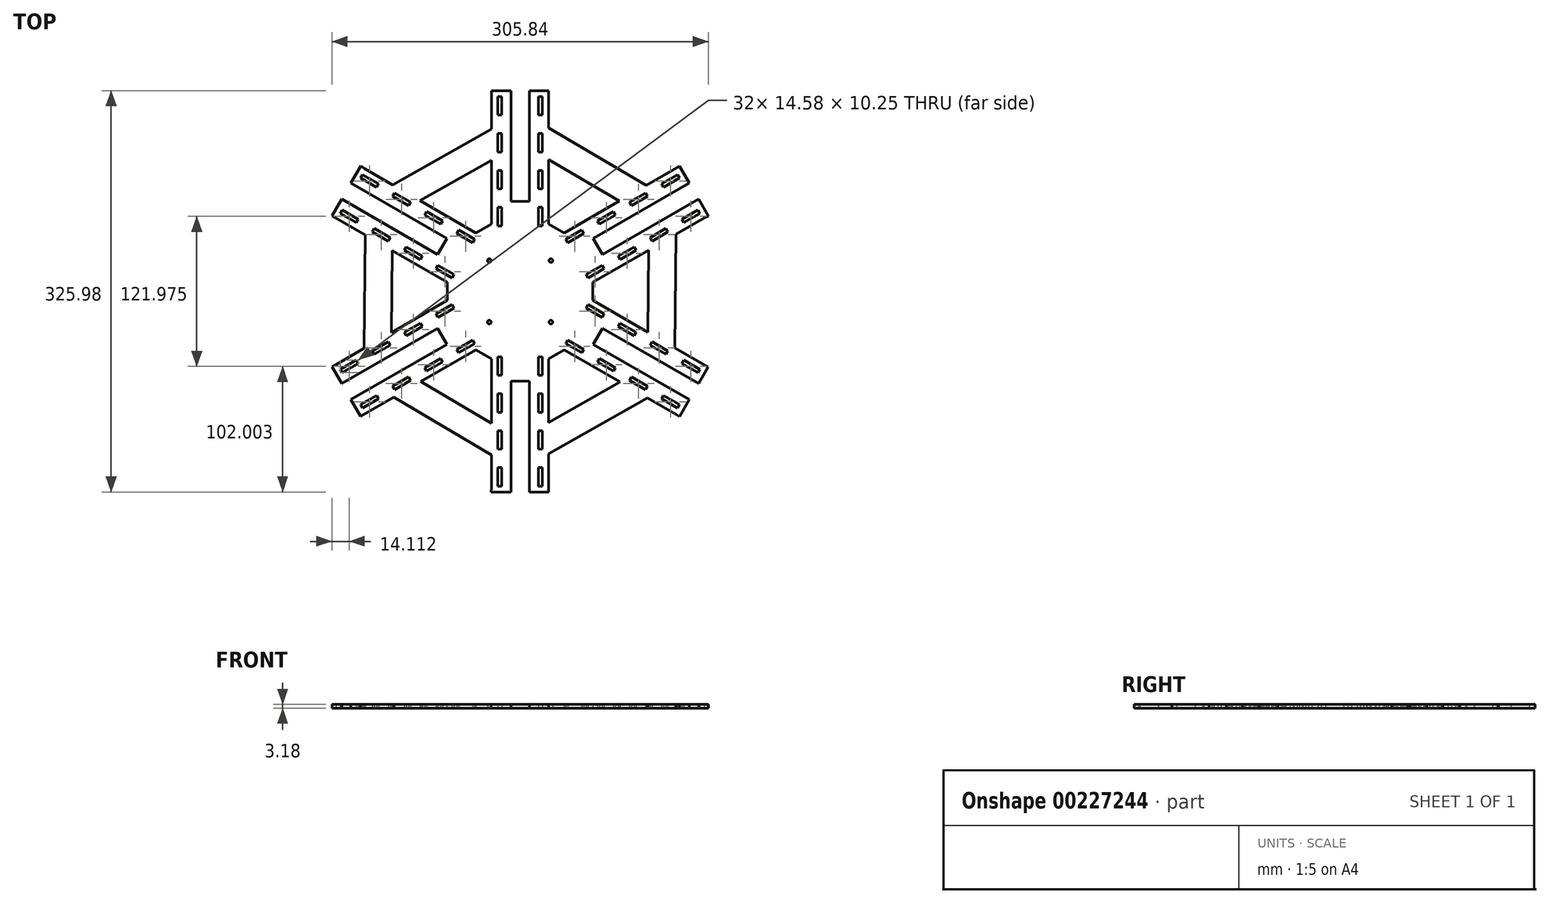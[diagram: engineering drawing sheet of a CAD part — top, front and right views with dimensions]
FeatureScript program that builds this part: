
annotation { "Feature Type Name" : "Feature", "Feature Type Description" : "" }
export const myFeature = defineFeature(function(context is Context, id is Id, definition is map)
    precondition{}
    {
        {
            var Q0;
            Q0=qCreatedBy(makeId("Top.planeOp"),FACE);
            var sketch = newSketch(context, id + "F0", { "sketchPlane" : qUnion([Q0])});
            skCircle(sketch, "E0.cCircle", {"center": v(0, 0) * mm, "radius": 173.2 * mm, "construction": true});
            skLineSegment(sketch, "E0.0", {"start": v(100, -173.2) * mm, "end": v(-100, -173.2) * mm});
            skLineSegment(sketch, "E0.1", {"start": v(-100, -173.2) * mm, "end": v(-200, 0) * mm});
            skLineSegment(sketch, "E0.2", {"start": v(-200, 0) * mm, "end": v(-100, 173.2) * mm});
            skLineSegment(sketch, "E0.3", {"start": v(-100, 173.2) * mm, "end": v(100, 173.2) * mm});
            skLineSegment(sketch, "E0.4", {"start": v(100, 173.2) * mm, "end": v(200, 0) * mm});
            skLineSegment(sketch, "E0.5", {"start": v(200, 0) * mm, "end": v(100, -173.2) * mm});
            skPoint(sketch, "E0.0.midPoint", {"position": v(0, -173.2) * mm});
            skLineSegment(sketch, "E1.bottom", {"start": v(-15, 143.2) * mm, "end": v(-18.18, 143.2) * mm});
            skLineSegment(sketch, "E1.top", {"start": v(-15, 158.2) * mm, "end": v(-18.18, 158.2) * mm});
            skLineSegment(sketch, "E1.left", {"start": v(-15, 143.2) * mm, "end": v(-15, 158.2) * mm});
            skLineSegment(sketch, "E1.right", {"start": v(-18.18, 143.2) * mm, "end": v(-18.18, 158.2) * mm});
            skPoint(sketch, "E1.middle", {"position": v(-16.59, 150.7) * mm});
            skPoint(sketch, "E2.0.1.0", {"position": v(-16.59, 120.7) * mm});
            skLineSegment(sketch, "E2.0.1.1", {"start": v(-18.18, 113.2) * mm, "end": v(-18.18, 128.2) * mm});
            skLineSegment(sketch, "E2.0.1.2", {"start": v(-15, 113.2) * mm, "end": v(-15, 128.2) * mm});
            skLineSegment(sketch, "E2.0.1.3", {"start": v(-15, 128.2) * mm, "end": v(-18.18, 128.2) * mm});
            skLineSegment(sketch, "E2.0.1.4", {"start": v(-15, 113.2) * mm, "end": v(-18.18, 113.2) * mm});
            skPoint(sketch, "E2.1.0.0", {"position": v(16.59, 150.7) * mm});
            skLineSegment(sketch, "E2.1.0.1", {"start": v(15, 143.2) * mm, "end": v(15, 158.2) * mm});
            skLineSegment(sketch, "E2.1.0.2", {"start": v(18.17, 143.2) * mm, "end": v(18.17, 158.2) * mm});
            skLineSegment(sketch, "E2.1.0.3", {"start": v(18.17, 158.2) * mm, "end": v(15, 158.2) * mm});
            skLineSegment(sketch, "E2.1.0.4", {"start": v(18.17, 143.2) * mm, "end": v(15, 143.2) * mm});
            skPoint(sketch, "E2.1.1.0", {"position": v(16.59, 120.7) * mm});
            skLineSegment(sketch, "E2.1.1.1", {"start": v(15, 113.2) * mm, "end": v(15, 128.2) * mm});
            skLineSegment(sketch, "E2.1.1.2", {"start": v(18.17, 113.2) * mm, "end": v(18.17, 128.2) * mm});
            skLineSegment(sketch, "E2.1.1.3", {"start": v(18.17, 128.2) * mm, "end": v(15, 128.2) * mm});
            skLineSegment(sketch, "E2.1.1.4", {"start": v(18.17, 113.2) * mm, "end": v(15, 113.2) * mm});
            skLineSegment(sketch, "E2.direction1", {"start": v(-18.18, 143.2) * mm, "end": v(15, 143.2) * mm, "construction": true});
            skLineSegment(sketch, "E2.direction2", {"start": v(-18.18, 143.2) * mm, "end": v(-18.18, 113.2) * mm, "construction": true});
            skLineSegment(sketch, "E3.1.0", {"start": v(-116.52, 84.6) * mm, "end": v(-129.5, 92.1) * mm});
            skLineSegment(sketch, "E3.1.1", {"start": v(-114.93, 87.34) * mm, "end": v(-127.92, 94.84) * mm});
            skPoint(sketch, "E3.1.2", {"position": v(-138.8, 60.99) * mm});
            skLineSegment(sketch, "E3.1.3", {"start": v(-133.1, 55.86) * mm, "end": v(-146.1, 63.36) * mm});
            skLineSegment(sketch, "E3.1.4", {"start": v(-131.52, 58.61) * mm, "end": v(-144.5, 66.11) * mm});
            skLineSegment(sketch, "E3.1.5", {"start": v(-107.13, 40.86) * mm, "end": v(-120.12, 48.36) * mm});
            skLineSegment(sketch, "E3.1.6", {"start": v(-133.1, 55.86) * mm, "end": v(-116.52, 84.6) * mm, "construction": true});
            skLineSegment(sketch, "E3.1.7", {"start": v(-105.54, 43.61) * mm, "end": v(-118.53, 51.11) * mm});
            skPoint(sketch, "E3.1.8", {"position": v(-122.22, 89.72) * mm});
            skLineSegment(sketch, "E3.1.9", {"start": v(-88.95, 72.34) * mm, "end": v(-101.94, 79.84) * mm});
            skLineSegment(sketch, "E3.1.10", {"start": v(-90.54, 69.6) * mm, "end": v(-103.53, 77.1) * mm});
            skLineSegment(sketch, "E3.1.11", {"start": v(-133.1, 55.86) * mm, "end": v(-107.13, 40.86) * mm, "construction": true});
            skPoint(sketch, "E3.1.12", {"position": v(-112.83, 45.99) * mm});
            skPoint(sketch, "E3.1.13", {"position": v(-96.24, 74.72) * mm});
            skLineSegment(sketch, "E3.1.14", {"start": v(-131.52, 58.61) * mm, "end": v(-133.1, 55.86) * mm});
            skLineSegment(sketch, "E3.1.15", {"start": v(-105.54, 43.61) * mm, "end": v(-107.13, 40.86) * mm});
            skLineSegment(sketch, "E3.1.16", {"start": v(-88.95, 72.34) * mm, "end": v(-90.54, 69.6) * mm});
            skLineSegment(sketch, "E3.1.17", {"start": v(-144.5, 66.11) * mm, "end": v(-146.1, 63.36) * mm});
            skLineSegment(sketch, "E3.1.18", {"start": v(-114.93, 87.34) * mm, "end": v(-116.52, 84.6) * mm});
            skLineSegment(sketch, "E3.1.19", {"start": v(-118.53, 51.11) * mm, "end": v(-120.12, 48.36) * mm});
            skLineSegment(sketch, "E3.1.20", {"start": v(-127.92, 94.84) * mm, "end": v(-129.5, 92.1) * mm});
            skLineSegment(sketch, "E3.1.21", {"start": v(-101.94, 79.84) * mm, "end": v(-103.53, 77.1) * mm});
            skLineSegment(sketch, "E3.2.0", {"start": v(-131.52, -58.61) * mm, "end": v(-144.5, -66.11) * mm});
            skLineSegment(sketch, "E3.2.1", {"start": v(-133.1, -55.86) * mm, "end": v(-146.1, -63.36) * mm});
            skPoint(sketch, "E3.2.2", {"position": v(-122.22, -89.72) * mm});
            skLineSegment(sketch, "E3.2.3", {"start": v(-114.93, -87.34) * mm, "end": v(-127.92, -94.84) * mm});
            skLineSegment(sketch, "E3.2.4", {"start": v(-116.52, -84.6) * mm, "end": v(-129.5, -92.1) * mm});
            skLineSegment(sketch, "E3.2.5", {"start": v(-88.95, -72.34) * mm, "end": v(-101.94, -79.84) * mm});
            skLineSegment(sketch, "E3.2.6", {"start": v(-114.93, -87.34) * mm, "end": v(-131.52, -58.61) * mm, "construction": true});
            skLineSegment(sketch, "E3.2.7", {"start": v(-90.54, -69.6) * mm, "end": v(-103.53, -77.1) * mm});
            skPoint(sketch, "E3.2.8", {"position": v(-138.8, -60.99) * mm});
            skLineSegment(sketch, "E3.2.9", {"start": v(-107.13, -40.86) * mm, "end": v(-120.12, -48.36) * mm});
            skLineSegment(sketch, "E3.2.10", {"start": v(-105.54, -43.61) * mm, "end": v(-118.53, -51.11) * mm});
            skLineSegment(sketch, "E3.2.11", {"start": v(-114.93, -87.34) * mm, "end": v(-88.95, -72.34) * mm, "construction": true});
            skPoint(sketch, "E3.2.12", {"position": v(-96.24, -74.72) * mm});
            skPoint(sketch, "E3.2.13", {"position": v(-112.83, -45.99) * mm});
            skLineSegment(sketch, "E3.2.14", {"start": v(-116.52, -84.6) * mm, "end": v(-114.93, -87.34) * mm});
            skLineSegment(sketch, "E3.2.15", {"start": v(-90.54, -69.6) * mm, "end": v(-88.95, -72.34) * mm});
            skLineSegment(sketch, "E3.2.16", {"start": v(-107.13, -40.86) * mm, "end": v(-105.54, -43.61) * mm});
            skLineSegment(sketch, "E3.2.17", {"start": v(-129.5, -92.1) * mm, "end": v(-127.92, -94.84) * mm});
            skLineSegment(sketch, "E3.2.18", {"start": v(-133.1, -55.86) * mm, "end": v(-131.52, -58.61) * mm});
            skLineSegment(sketch, "E3.2.19", {"start": v(-103.53, -77.1) * mm, "end": v(-101.94, -79.84) * mm});
            skLineSegment(sketch, "E3.2.20", {"start": v(-146.1, -63.36) * mm, "end": v(-144.5, -66.11) * mm});
            skLineSegment(sketch, "E3.2.21", {"start": v(-120.12, -48.36) * mm, "end": v(-118.53, -51.11) * mm});
            skLineSegment(sketch, "E3.3.0", {"start": v(-15, -143.2) * mm, "end": v(-15, -158.2) * mm});
            skLineSegment(sketch, "E3.3.1", {"start": v(-18.17, -143.2) * mm, "end": v(-18.17, -158.2) * mm});
            skPoint(sketch, "E3.3.2", {"position": v(16.59, -150.7) * mm});
            skLineSegment(sketch, "E3.3.3", {"start": v(18.18, -143.2) * mm, "end": v(18.18, -158.2) * mm});
            skLineSegment(sketch, "E3.3.4", {"start": v(15, -143.2) * mm, "end": v(15, -158.2) * mm});
            skLineSegment(sketch, "E3.3.5", {"start": v(18.18, -113.2) * mm, "end": v(18.18, -128.2) * mm});
            skLineSegment(sketch, "E3.3.6", {"start": v(18.17, -143.2) * mm, "end": v(-15, -143.2) * mm, "construction": true});
            skLineSegment(sketch, "E3.3.7", {"start": v(15, -113.2) * mm, "end": v(15, -128.2) * mm});
            skPoint(sketch, "E3.3.8", {"position": v(-16.59, -150.7) * mm});
            skLineSegment(sketch, "E3.3.9", {"start": v(-18.17, -113.2) * mm, "end": v(-18.17, -128.2) * mm});
            skLineSegment(sketch, "E3.3.10", {"start": v(-15, -113.2) * mm, "end": v(-15, -128.2) * mm});
            skLineSegment(sketch, "E3.3.11", {"start": v(18.18, -143.2) * mm, "end": v(18.18, -113.2) * mm, "construction": true});
            skPoint(sketch, "E3.3.12", {"position": v(16.59, -120.7) * mm});
            skPoint(sketch, "E3.3.13", {"position": v(-16.59, -120.7) * mm});
            skLineSegment(sketch, "E3.3.14", {"start": v(15, -143.2) * mm, "end": v(18.17, -143.2) * mm});
            skLineSegment(sketch, "E3.3.15", {"start": v(15, -113.2) * mm, "end": v(18.17, -113.2) * mm});
            skLineSegment(sketch, "E3.3.16", {"start": v(-18.18, -113.2) * mm, "end": v(-15, -113.2) * mm});
            skLineSegment(sketch, "E3.3.17", {"start": v(15, -158.2) * mm, "end": v(18.17, -158.2) * mm});
            skLineSegment(sketch, "E3.3.18", {"start": v(-18.18, -143.2) * mm, "end": v(-15, -143.2) * mm});
            skLineSegment(sketch, "E3.3.19", {"start": v(15, -128.2) * mm, "end": v(18.17, -128.2) * mm});
            skLineSegment(sketch, "E3.3.20", {"start": v(-18.18, -158.2) * mm, "end": v(-15, -158.2) * mm});
            skLineSegment(sketch, "E3.3.21", {"start": v(-18.18, -128.2) * mm, "end": v(-15, -128.2) * mm});
            skLineSegment(sketch, "E3.4.0", {"start": v(116.52, -84.6) * mm, "end": v(129.5, -92.1) * mm});
            skLineSegment(sketch, "E3.4.1", {"start": v(114.93, -87.34) * mm, "end": v(127.92, -94.84) * mm});
            skPoint(sketch, "E3.4.2", {"position": v(138.8, -60.99) * mm});
            skLineSegment(sketch, "E3.4.3", {"start": v(133.1, -55.86) * mm, "end": v(146.1, -63.36) * mm});
            skLineSegment(sketch, "E3.4.4", {"start": v(131.52, -58.61) * mm, "end": v(144.5, -66.11) * mm});
            skLineSegment(sketch, "E3.4.5", {"start": v(107.13, -40.86) * mm, "end": v(120.12, -48.36) * mm});
            skLineSegment(sketch, "E3.4.6", {"start": v(133.1, -55.86) * mm, "end": v(116.52, -84.6) * mm, "construction": true});
            skLineSegment(sketch, "E3.4.7", {"start": v(105.54, -43.61) * mm, "end": v(118.53, -51.11) * mm});
            skPoint(sketch, "E3.4.8", {"position": v(122.22, -89.72) * mm});
            skLineSegment(sketch, "E3.4.9", {"start": v(88.95, -72.34) * mm, "end": v(101.94, -79.84) * mm});
            skLineSegment(sketch, "E3.4.10", {"start": v(90.54, -69.6) * mm, "end": v(103.53, -77.1) * mm});
            skLineSegment(sketch, "E3.4.11", {"start": v(133.1, -55.86) * mm, "end": v(107.13, -40.86) * mm, "construction": true});
            skPoint(sketch, "E3.4.12", {"position": v(112.83, -45.99) * mm});
            skPoint(sketch, "E3.4.13", {"position": v(96.24, -74.72) * mm});
            skLineSegment(sketch, "E3.4.14", {"start": v(131.52, -58.61) * mm, "end": v(133.1, -55.86) * mm});
            skLineSegment(sketch, "E3.4.15", {"start": v(105.54, -43.61) * mm, "end": v(107.13, -40.86) * mm});
            skLineSegment(sketch, "E3.4.16", {"start": v(88.95, -72.34) * mm, "end": v(90.54, -69.6) * mm});
            skLineSegment(sketch, "E3.4.17", {"start": v(144.5, -66.11) * mm, "end": v(146.1, -63.36) * mm});
            skLineSegment(sketch, "E3.4.18", {"start": v(114.93, -87.34) * mm, "end": v(116.52, -84.6) * mm});
            skLineSegment(sketch, "E3.4.19", {"start": v(118.53, -51.11) * mm, "end": v(120.12, -48.36) * mm});
            skLineSegment(sketch, "E3.4.20", {"start": v(127.92, -94.84) * mm, "end": v(129.5, -92.1) * mm});
            skLineSegment(sketch, "E3.4.21", {"start": v(101.94, -79.84) * mm, "end": v(103.53, -77.1) * mm});
            skLineSegment(sketch, "E3.5.0", {"start": v(131.52, 58.61) * mm, "end": v(144.5, 66.11) * mm});
            skLineSegment(sketch, "E3.5.1", {"start": v(133.1, 55.86) * mm, "end": v(146.1, 63.36) * mm});
            skPoint(sketch, "E3.5.2", {"position": v(122.22, 89.72) * mm});
            skLineSegment(sketch, "E3.5.3", {"start": v(114.93, 87.34) * mm, "end": v(127.92, 94.84) * mm});
            skLineSegment(sketch, "E3.5.4", {"start": v(116.52, 84.6) * mm, "end": v(129.5, 92.1) * mm});
            skLineSegment(sketch, "E3.5.5", {"start": v(88.95, 72.34) * mm, "end": v(101.94, 79.84) * mm});
            skLineSegment(sketch, "E3.5.6", {"start": v(114.93, 87.34) * mm, "end": v(131.52, 58.61) * mm, "construction": true});
            skLineSegment(sketch, "E3.5.7", {"start": v(90.54, 69.6) * mm, "end": v(103.53, 77.1) * mm});
            skPoint(sketch, "E3.5.8", {"position": v(138.8, 60.99) * mm});
            skLineSegment(sketch, "E3.5.9", {"start": v(107.13, 40.86) * mm, "end": v(120.12, 48.36) * mm});
            skLineSegment(sketch, "E3.5.10", {"start": v(105.54, 43.61) * mm, "end": v(118.53, 51.11) * mm});
            skLineSegment(sketch, "E3.5.11", {"start": v(114.93, 87.34) * mm, "end": v(88.95, 72.34) * mm, "construction": true});
            skPoint(sketch, "E3.5.12", {"position": v(96.24, 74.72) * mm});
            skPoint(sketch, "E3.5.13", {"position": v(112.83, 45.99) * mm});
            skLineSegment(sketch, "E3.5.14", {"start": v(116.52, 84.6) * mm, "end": v(114.93, 87.34) * mm});
            skLineSegment(sketch, "E3.5.15", {"start": v(90.54, 69.6) * mm, "end": v(88.95, 72.34) * mm});
            skLineSegment(sketch, "E3.5.16", {"start": v(107.13, 40.86) * mm, "end": v(105.54, 43.61) * mm});
            skLineSegment(sketch, "E3.5.17", {"start": v(129.5, 92.1) * mm, "end": v(127.92, 94.84) * mm});
            skLineSegment(sketch, "E3.5.18", {"start": v(133.1, 55.86) * mm, "end": v(131.52, 58.61) * mm});
            skLineSegment(sketch, "E3.5.19", {"start": v(103.53, 77.1) * mm, "end": v(101.94, 79.84) * mm});
            skLineSegment(sketch, "E3.5.20", {"start": v(146.1, 63.36) * mm, "end": v(144.5, 66.11) * mm});
            skLineSegment(sketch, "E3.5.21", {"start": v(120.12, 48.36) * mm, "end": v(118.53, 51.11) * mm});
            skLineSegment(sketch, "E4.bottom", {"start": v(25, -25) * mm, "end": v(-25, -25) * mm, "construction": true});
            skLineSegment(sketch, "E4.top", {"start": v(25, 25) * mm, "end": v(-25, 25) * mm, "construction": true});
            skLineSegment(sketch, "E4.left", {"start": v(25, -25) * mm, "end": v(25, 25) * mm, "construction": true});
            skLineSegment(sketch, "E4.right", {"start": v(-25, -25) * mm, "end": v(-25, 25) * mm, "construction": true});
            skCircle(sketch, "E5", {"center": v(-25, 25) * mm, "radius": 1.5 * mm});
            skCircle(sketch, "E6.1.0", {"center": v(-25, -25) * mm, "radius": 1.5 * mm});
            skCircle(sketch, "E6.2.0", {"center": v(25, -25) * mm, "radius": 1.5 * mm});
            skCircle(sketch, "E6.3.0", {"center": v(25, 25) * mm, "radius": 1.5 * mm});
            skPoint(sketch, "E7.0.0.2", {"position": v(-16.59, 90.7) * mm});
            skLineSegment(sketch, "E7.1.0.2", {"start": v(-18.18, 83.2) * mm, "end": v(-18.18, 98.2) * mm});
            skLineSegment(sketch, "E7.4.0.2", {"start": v(-15, 83.2) * mm, "end": v(-15, 98.2) * mm});
            skLineSegment(sketch, "E7.7.0.2", {"start": v(-15, 98.2) * mm, "end": v(-18.18, 98.2) * mm});
            skLineSegment(sketch, "E7.10.0.2", {"start": v(-15, 83.2) * mm, "end": v(-18.18, 83.2) * mm});
            skPoint(sketch, "E7.0.1.2", {"position": v(16.59, 90.7) * mm});
            skLineSegment(sketch, "E7.1.1.2", {"start": v(15, 83.2) * mm, "end": v(15, 98.2) * mm});
            skLineSegment(sketch, "E7.4.1.2", {"start": v(18.17, 83.2) * mm, "end": v(18.17, 98.2) * mm});
            skLineSegment(sketch, "E7.7.1.2", {"start": v(18.17, 98.2) * mm, "end": v(15, 98.2) * mm});
            skLineSegment(sketch, "E7.10.1.2", {"start": v(18.17, 83.2) * mm, "end": v(15, 83.2) * mm});
            skPoint(sketch, "E8.0.0.3", {"position": v(-16.59, 60.7) * mm});
            skLineSegment(sketch, "E8.1.0.3", {"start": v(-18.18, 53.2) * mm, "end": v(-18.18, 68.2) * mm});
            skLineSegment(sketch, "E8.4.0.3", {"start": v(-15, 53.2) * mm, "end": v(-15, 68.2) * mm});
            skLineSegment(sketch, "E8.7.0.3", {"start": v(-15, 68.2) * mm, "end": v(-18.18, 68.2) * mm});
            skLineSegment(sketch, "E8.10.0.3", {"start": v(-15, 53.2) * mm, "end": v(-18.18, 53.2) * mm});
            skPoint(sketch, "E8.0.1.3", {"position": v(16.59, 60.7) * mm});
            skLineSegment(sketch, "E8.1.1.3", {"start": v(15, 53.2) * mm, "end": v(15, 68.2) * mm});
            skLineSegment(sketch, "E8.4.1.3", {"start": v(18.17, 53.2) * mm, "end": v(18.17, 68.2) * mm});
            skLineSegment(sketch, "E8.7.1.3", {"start": v(18.17, 68.2) * mm, "end": v(15, 68.2) * mm});
            skLineSegment(sketch, "E8.10.1.3", {"start": v(18.18, 53.2) * mm, "end": v(15, 53.2) * mm});
            skPoint(sketch, "E9.1.0", {"position": v(-60.87, 15.99) * mm});
            skPoint(sketch, "E9.1.1", {"position": v(-86.85, 30.99) * mm});
            skPoint(sketch, "E9.1.2", {"position": v(-44.28, 44.72) * mm});
            skPoint(sketch, "E9.1.3", {"position": v(-70.26, 59.72) * mm});
            skLineSegment(sketch, "E9.1.4", {"start": v(-55.16, 10.86) * mm, "end": v(-68.15, 18.36) * mm});
            skLineSegment(sketch, "E9.1.5", {"start": v(-36.99, 42.34) * mm, "end": v(-49.98, 49.84) * mm});
            skLineSegment(sketch, "E9.1.6", {"start": v(-79.56, 28.61) * mm, "end": v(-92.55, 36.11) * mm});
            skLineSegment(sketch, "E9.1.7", {"start": v(-64.56, 54.6) * mm, "end": v(-77.55, 62.1) * mm});
            skLineSegment(sketch, "E9.1.8", {"start": v(-62.97, 57.34) * mm, "end": v(-75.96, 64.84) * mm});
            skLineSegment(sketch, "E9.1.9", {"start": v(-53.58, 13.61) * mm, "end": v(-66.57, 21.11) * mm});
            skLineSegment(sketch, "E9.1.10", {"start": v(-38.58, 39.6) * mm, "end": v(-51.57, 47.1) * mm});
            skLineSegment(sketch, "E9.1.11", {"start": v(-81.15, 25.86) * mm, "end": v(-94.14, 33.36) * mm});
            skLineSegment(sketch, "E9.1.12", {"start": v(-79.56, 28.61) * mm, "end": v(-81.15, 25.86) * mm});
            skLineSegment(sketch, "E9.1.13", {"start": v(-62.97, 57.34) * mm, "end": v(-64.56, 54.6) * mm});
            skLineSegment(sketch, "E9.1.14", {"start": v(-49.98, 49.84) * mm, "end": v(-51.57, 47.1) * mm});
            skLineSegment(sketch, "E9.1.15", {"start": v(-36.99, 42.34) * mm, "end": v(-38.58, 39.6) * mm});
            skLineSegment(sketch, "E9.1.16", {"start": v(-75.96, 64.84) * mm, "end": v(-77.55, 62.1) * mm});
            skLineSegment(sketch, "E9.1.17", {"start": v(-92.55, 36.11) * mm, "end": v(-94.14, 33.36) * mm});
            skLineSegment(sketch, "E9.1.18", {"start": v(-53.58, 13.61) * mm, "end": v(-55.16, 10.86) * mm});
            skLineSegment(sketch, "E9.1.19", {"start": v(-66.57, 21.11) * mm, "end": v(-68.15, 18.36) * mm});
            skPoint(sketch, "E9.2.0", {"position": v(-44.28, -44.72) * mm});
            skPoint(sketch, "E9.2.1", {"position": v(-70.26, -59.72) * mm});
            skPoint(sketch, "E9.2.2", {"position": v(-60.87, -15.99) * mm});
            skPoint(sketch, "E9.2.3", {"position": v(-86.85, -30.99) * mm});
            skLineSegment(sketch, "E9.2.4", {"start": v(-36.99, -42.34) * mm, "end": v(-49.98, -49.84) * mm});
            skLineSegment(sketch, "E9.2.5", {"start": v(-55.16, -10.86) * mm, "end": v(-68.15, -18.36) * mm});
            skLineSegment(sketch, "E9.2.6", {"start": v(-64.56, -54.6) * mm, "end": v(-77.55, -62.1) * mm});
            skLineSegment(sketch, "E9.2.7", {"start": v(-79.56, -28.61) * mm, "end": v(-92.55, -36.11) * mm});
            skLineSegment(sketch, "E9.2.8", {"start": v(-81.15, -25.86) * mm, "end": v(-94.14, -33.36) * mm});
            skLineSegment(sketch, "E9.2.9", {"start": v(-38.58, -39.6) * mm, "end": v(-51.57, -47.1) * mm});
            skLineSegment(sketch, "E9.2.10", {"start": v(-53.58, -13.61) * mm, "end": v(-66.57, -21.11) * mm});
            skLineSegment(sketch, "E9.2.11", {"start": v(-62.97, -57.34) * mm, "end": v(-75.96, -64.84) * mm});
            skLineSegment(sketch, "E9.2.12", {"start": v(-64.56, -54.6) * mm, "end": v(-62.97, -57.34) * mm});
            skLineSegment(sketch, "E9.2.13", {"start": v(-81.15, -25.86) * mm, "end": v(-79.56, -28.61) * mm});
            skLineSegment(sketch, "E9.2.14", {"start": v(-68.15, -18.36) * mm, "end": v(-66.57, -21.11) * mm});
            skLineSegment(sketch, "E9.2.15", {"start": v(-55.16, -10.86) * mm, "end": v(-53.58, -13.61) * mm});
            skLineSegment(sketch, "E9.2.16", {"start": v(-94.14, -33.36) * mm, "end": v(-92.55, -36.11) * mm});
            skLineSegment(sketch, "E9.2.17", {"start": v(-77.55, -62.1) * mm, "end": v(-75.96, -64.84) * mm});
            skLineSegment(sketch, "E9.2.18", {"start": v(-38.58, -39.6) * mm, "end": v(-36.99, -42.34) * mm});
            skLineSegment(sketch, "E9.2.19", {"start": v(-51.57, -47.1) * mm, "end": v(-49.98, -49.84) * mm});
            skPoint(sketch, "E9.3.0", {"position": v(16.59, -60.7) * mm});
            skPoint(sketch, "E9.3.1", {"position": v(16.59, -90.7) * mm});
            skPoint(sketch, "E9.3.2", {"position": v(-16.59, -60.7) * mm});
            skPoint(sketch, "E9.3.3", {"position": v(-16.59, -90.7) * mm});
            skLineSegment(sketch, "E9.3.4", {"start": v(18.18, -53.2) * mm, "end": v(18.18, -68.2) * mm});
            skLineSegment(sketch, "E9.3.5", {"start": v(-18.17, -53.2) * mm, "end": v(-18.17, -68.2) * mm});
            skLineSegment(sketch, "E9.3.6", {"start": v(15, -83.2) * mm, "end": v(15, -98.2) * mm});
            skLineSegment(sketch, "E9.3.7", {"start": v(-15, -83.2) * mm, "end": v(-15, -98.2) * mm});
            skLineSegment(sketch, "E9.3.8", {"start": v(-18.17, -83.2) * mm, "end": v(-18.17, -98.2) * mm});
            skLineSegment(sketch, "E9.3.9", {"start": v(15, -53.2) * mm, "end": v(15, -68.2) * mm});
            skLineSegment(sketch, "E9.3.10", {"start": v(-15, -53.2) * mm, "end": v(-15, -68.2) * mm});
            skLineSegment(sketch, "E9.3.11", {"start": v(18.18, -83.2) * mm, "end": v(18.18, -98.2) * mm});
            skLineSegment(sketch, "E9.3.12", {"start": v(15, -83.2) * mm, "end": v(18.17, -83.2) * mm});
            skLineSegment(sketch, "E9.3.13", {"start": v(-18.18, -83.2) * mm, "end": v(-15, -83.2) * mm});
            skLineSegment(sketch, "E9.3.14", {"start": v(-18.18, -68.2) * mm, "end": v(-15, -68.2) * mm});
            skLineSegment(sketch, "E9.3.15", {"start": v(-18.18, -53.2) * mm, "end": v(-15, -53.2) * mm});
            skLineSegment(sketch, "E9.3.16", {"start": v(-18.18, -98.2) * mm, "end": v(-15, -98.2) * mm});
            skLineSegment(sketch, "E9.3.17", {"start": v(15, -98.2) * mm, "end": v(18.17, -98.2) * mm});
            skLineSegment(sketch, "E9.3.18", {"start": v(15, -53.2) * mm, "end": v(18.17, -53.2) * mm});
            skLineSegment(sketch, "E9.3.19", {"start": v(15, -68.2) * mm, "end": v(18.17, -68.2) * mm});
            skPoint(sketch, "E9.4.0", {"position": v(60.87, -15.99) * mm});
            skPoint(sketch, "E9.4.1", {"position": v(86.85, -30.99) * mm});
            skPoint(sketch, "E9.4.2", {"position": v(44.28, -44.72) * mm});
            skPoint(sketch, "E9.4.3", {"position": v(70.26, -59.72) * mm});
            skLineSegment(sketch, "E9.4.4", {"start": v(55.16, -10.86) * mm, "end": v(68.15, -18.36) * mm});
            skLineSegment(sketch, "E9.4.5", {"start": v(36.99, -42.34) * mm, "end": v(49.98, -49.84) * mm});
            skLineSegment(sketch, "E9.4.6", {"start": v(79.56, -28.61) * mm, "end": v(92.55, -36.11) * mm});
            skLineSegment(sketch, "E9.4.7", {"start": v(64.56, -54.6) * mm, "end": v(77.55, -62.1) * mm});
            skLineSegment(sketch, "E9.4.8", {"start": v(62.97, -57.34) * mm, "end": v(75.96, -64.84) * mm});
            skLineSegment(sketch, "E9.4.9", {"start": v(53.58, -13.61) * mm, "end": v(66.57, -21.11) * mm});
            skLineSegment(sketch, "E9.4.10", {"start": v(38.58, -39.6) * mm, "end": v(51.57, -47.1) * mm});
            skLineSegment(sketch, "E9.4.11", {"start": v(81.15, -25.86) * mm, "end": v(94.14, -33.36) * mm});
            skLineSegment(sketch, "E9.4.12", {"start": v(79.56, -28.61) * mm, "end": v(81.15, -25.86) * mm});
            skLineSegment(sketch, "E9.4.13", {"start": v(62.97, -57.34) * mm, "end": v(64.56, -54.6) * mm});
            skLineSegment(sketch, "E9.4.14", {"start": v(49.98, -49.84) * mm, "end": v(51.57, -47.1) * mm});
            skLineSegment(sketch, "E9.4.15", {"start": v(36.99, -42.34) * mm, "end": v(38.58, -39.6) * mm});
            skLineSegment(sketch, "E9.4.16", {"start": v(75.96, -64.84) * mm, "end": v(77.55, -62.1) * mm});
            skLineSegment(sketch, "E9.4.17", {"start": v(92.55, -36.11) * mm, "end": v(94.14, -33.36) * mm});
            skLineSegment(sketch, "E9.4.18", {"start": v(53.58, -13.61) * mm, "end": v(55.16, -10.86) * mm});
            skLineSegment(sketch, "E9.4.19", {"start": v(66.57, -21.11) * mm, "end": v(68.15, -18.36) * mm});
            skPoint(sketch, "E9.5.0", {"position": v(44.28, 44.72) * mm});
            skPoint(sketch, "E9.5.1", {"position": v(70.26, 59.72) * mm});
            skPoint(sketch, "E9.5.2", {"position": v(60.87, 15.99) * mm});
            skPoint(sketch, "E9.5.3", {"position": v(86.85, 30.99) * mm});
            skLineSegment(sketch, "E9.5.4", {"start": v(36.99, 42.34) * mm, "end": v(49.98, 49.84) * mm});
            skLineSegment(sketch, "E9.5.5", {"start": v(55.16, 10.86) * mm, "end": v(68.15, 18.36) * mm});
            skLineSegment(sketch, "E9.5.6", {"start": v(64.56, 54.6) * mm, "end": v(77.55, 62.1) * mm});
            skLineSegment(sketch, "E9.5.7", {"start": v(79.56, 28.61) * mm, "end": v(92.55, 36.11) * mm});
            skLineSegment(sketch, "E9.5.8", {"start": v(81.15, 25.86) * mm, "end": v(94.14, 33.36) * mm});
            skLineSegment(sketch, "E9.5.9", {"start": v(38.58, 39.6) * mm, "end": v(51.57, 47.1) * mm});
            skLineSegment(sketch, "E9.5.10", {"start": v(53.58, 13.61) * mm, "end": v(66.57, 21.11) * mm});
            skLineSegment(sketch, "E9.5.11", {"start": v(62.97, 57.34) * mm, "end": v(75.96, 64.84) * mm});
            skLineSegment(sketch, "E9.5.12", {"start": v(64.56, 54.6) * mm, "end": v(62.97, 57.34) * mm});
            skLineSegment(sketch, "E9.5.13", {"start": v(81.15, 25.86) * mm, "end": v(79.56, 28.61) * mm});
            skLineSegment(sketch, "E9.5.14", {"start": v(68.15, 18.36) * mm, "end": v(66.57, 21.11) * mm});
            skLineSegment(sketch, "E9.5.15", {"start": v(55.16, 10.86) * mm, "end": v(53.58, 13.61) * mm});
            skLineSegment(sketch, "E9.5.16", {"start": v(94.14, 33.36) * mm, "end": v(92.55, 36.11) * mm});
            skLineSegment(sketch, "E9.5.17", {"start": v(77.55, 62.1) * mm, "end": v(75.96, 64.84) * mm});
            skLineSegment(sketch, "E9.5.18", {"start": v(38.58, 39.6) * mm, "end": v(36.99, 42.34) * mm});
            skLineSegment(sketch, "E9.5.19", {"start": v(51.57, 47.1) * mm, "end": v(49.98, 49.84) * mm});
            skLineSegment(sketch, "E10", {"start": v(-126.5, 99.8) * mm, "end": v(-35.78, 47.42) * mm});
            skLineSegment(sketch, "E11", {"start": v(-35.78, 47.42) * mm, "end": v(-23.17, 54.7) * mm});
            skLineSegment(sketch, "E12", {"start": v(-23.18, 54.7) * mm, "end": v(-23.18, 158.2) * mm});
            skLineSegment(sketch, "E13", {"start": v(-23.17, 158.2) * mm, "end": v(-126.5, 99.8) * mm});
            skLineSegment(sketch, "E14.1.0", {"start": v(-148.6, 59.03) * mm, "end": v(-149.68, -59.66) * mm});
            skLineSegment(sketch, "E14.1.1", {"start": v(-58.95, 7.28) * mm, "end": v(-148.6, 59.03) * mm});
            skLineSegment(sketch, "E14.1.2", {"start": v(-149.68, -59.66) * mm, "end": v(-58.95, -7.28) * mm});
            skLineSegment(sketch, "E14.1.3", {"start": v(-58.95, -7.28) * mm, "end": v(-58.95, 7.28) * mm});
            skLineSegment(sketch, "E14.2.0", {"start": v(-125.42, -99.17) * mm, "end": v(-23.18, -159.46) * mm});
            skLineSegment(sketch, "E14.2.1", {"start": v(-35.78, -47.42) * mm, "end": v(-125.42, -99.17) * mm});
            skLineSegment(sketch, "E14.2.2", {"start": v(-23.18, -159.46) * mm, "end": v(-23.18, -54.7) * mm});
            skLineSegment(sketch, "E14.2.3", {"start": v(-23.18, -54.7) * mm, "end": v(-35.78, -47.42) * mm});
            skLineSegment(sketch, "E14.3.0", {"start": v(23.17, -158.2) * mm, "end": v(126.5, -99.8) * mm});
            skLineSegment(sketch, "E14.3.1", {"start": v(23.17, -54.7) * mm, "end": v(23.17, -158.2) * mm});
            skLineSegment(sketch, "E14.3.2", {"start": v(126.5, -99.8) * mm, "end": v(35.78, -47.42) * mm});
            skLineSegment(sketch, "E14.3.3", {"start": v(35.78, -47.42) * mm, "end": v(23.17, -54.7) * mm});
            skLineSegment(sketch, "E14.4.0", {"start": v(148.6, -59.03) * mm, "end": v(149.68, 59.66) * mm});
            skLineSegment(sketch, "E14.4.1", {"start": v(58.95, -7.28) * mm, "end": v(148.6, -59.03) * mm});
            skLineSegment(sketch, "E14.4.2", {"start": v(149.68, 59.66) * mm, "end": v(58.95, 7.28) * mm});
            skLineSegment(sketch, "E14.4.3", {"start": v(58.95, 7.28) * mm, "end": v(58.95, -7.28) * mm});
            skLineSegment(sketch, "E14.5.0", {"start": v(125.42, 99.17) * mm, "end": v(23.17, 159.46) * mm});
            skLineSegment(sketch, "E14.5.1", {"start": v(35.78, 47.42) * mm, "end": v(125.42, 99.17) * mm});
            skLineSegment(sketch, "E14.5.2", {"start": v(23.17, 159.46) * mm, "end": v(23.18, 54.7) * mm});
            skLineSegment(sketch, "E14.5.3", {"start": v(23.18, 54.7) * mm, "end": v(35.78, 47.42) * mm});
            skLineSegment(sketch, "E15", {"start": v(-103.5, 86.51) * mm, "end": v(-23.18, 131.91) * mm});
            skLineSegment(sketch, "E16", {"start": v(-23.18, 131.91) * mm, "end": v(-23.18, 106.45) * mm});
            skLineSegment(sketch, "E17", {"start": v(-23.18, 106.45) * mm, "end": v(-81.21, 73.65) * mm});
            skLineSegment(sketch, "E18.1.0", {"start": v(-126.67, -46.37) * mm, "end": v(-125.83, 45.89) * mm});
            skLineSegment(sketch, "E18.1.1", {"start": v(-103.77, 33.15) * mm, "end": v(-104.39, -33.5) * mm});
            skLineSegment(sketch, "E18.2.0", {"start": v(-23.18, -132.89) * mm, "end": v(-102.65, -86.03) * mm});
            skLineSegment(sketch, "E18.2.1", {"start": v(-80.6, -73.3) * mm, "end": v(-23.17, -107.15) * mm});
            skLineSegment(sketch, "E19.1.3.0", {"start": v(103.5, -86.51) * mm, "end": v(23.17, -131.91) * mm});
            skLineSegment(sketch, "E19.3.3.0", {"start": v(23.17, -106.45) * mm, "end": v(81.21, -73.65) * mm});
            skLineSegment(sketch, "E19.1.4.0", {"start": v(126.67, 46.37) * mm, "end": v(125.83, -45.89) * mm});
            skLineSegment(sketch, "E19.3.4.0", {"start": v(103.77, -33.15) * mm, "end": v(104.39, 33.5) * mm});
            skLineSegment(sketch, "E19.1.5.0", {"start": v(23.17, 132.89) * mm, "end": v(102.65, 86.03) * mm});
            skLineSegment(sketch, "E19.3.5.0", {"start": v(80.6, 73.3) * mm, "end": v(23.17, 107.15) * mm});
            skLineSegment(sketch, "E20", {"start": v(-148.6, 59.03) * mm, "end": v(-152.74, 61.42) * mm});
            skLineSegment(sketch, "E21", {"start": v(-152.74, 61.42) * mm, "end": v(-129.39, 101.87) * mm});
            skLineSegment(sketch, "E22", {"start": v(-129.39, 101.87) * mm, "end": v(-126.5, 99.8) * mm});
            skLineSegment(sketch, "E23.1.0", {"start": v(-129.57, -101.56) * mm, "end": v(-152.92, -61.12) * mm});
            skLineSegment(sketch, "E23.1.1", {"start": v(-152.92, -61.12) * mm, "end": v(-149.68, -59.66) * mm});
            skLineSegment(sketch, "E23.1.2", {"start": v(-125.42, -99.17) * mm, "end": v(-129.57, -101.56) * mm});
            skLineSegment(sketch, "E23.2.0", {"start": v(23.17, -162.99) * mm, "end": v(-23.53, -162.99) * mm});
            skLineSegment(sketch, "E23.2.1", {"start": v(-23.53, -162.99) * mm, "end": v(-23.18, -159.46) * mm});
            skLineSegment(sketch, "E23.2.2", {"start": v(23.17, -158.2) * mm, "end": v(23.17, -162.99) * mm});
            skLineSegment(sketch, "E23.3.0", {"start": v(152.74, -61.42) * mm, "end": v(129.39, -101.87) * mm});
            skLineSegment(sketch, "E23.3.1", {"start": v(129.39, -101.87) * mm, "end": v(126.5, -99.8) * mm});
            skLineSegment(sketch, "E23.3.2", {"start": v(148.6, -59.03) * mm, "end": v(152.74, -61.42) * mm});
            skLineSegment(sketch, "E23.4.0", {"start": v(129.57, 101.56) * mm, "end": v(152.92, 61.12) * mm});
            skLineSegment(sketch, "E23.4.1", {"start": v(152.92, 61.12) * mm, "end": v(149.68, 59.66) * mm});
            skLineSegment(sketch, "E23.4.2", {"start": v(125.42, 99.17) * mm, "end": v(129.57, 101.56) * mm});
            skLineSegment(sketch, "E23.5.2", {"start": v(-23.18, 158.2) * mm, "end": v(-23.18, 162.99) * mm});
            skLineSegment(sketch, "E24", {"start": v(23.17, 159.46) * mm, "end": v(23.17, 162.99) * mm});
            skLineSegment(sketch, "E25", {"start": v(23.17, 162.99) * mm, "end": v(-23.18, 162.99) * mm});
            skSolve(sketch);
        }
        {
            var Q0;
            {var subQ0=sQuery(id+"F0.wireOp",EDGE,"E15");Q0=makeQuery(id+"F0.imprint","IMPRINT",FACE,{"disambiguationData":[TD([[makeQuery(id+"F0.imprint","IMPRINT",EDGE,{"derivedFrom":subQ0}),-1.0]])]});}
            var Q1;
            {var subQ0=sQuery(id+"F0.wireOp",EDGE,"E18.1.0");Q1=makeQuery(id+"F0.imprint","IMPRINT",FACE,{"disambiguationData":[TD([[makeQuery(id+"F0.imprint","IMPRINT",EDGE,{"derivedFrom":subQ0}),-1.0]])]});}
            var Q2;
            {var subQ0=sQuery(id+"F0.wireOp",EDGE,"E18.2.0");Q2=makeQuery(id+"F0.imprint","IMPRINT",FACE,{"disambiguationData":[TD([[makeQuery(id+"F0.imprint","IMPRINT",EDGE,{"derivedFrom":subQ0}),-1.0]])]});}
            var Q3;
            {var subQ0=sQuery(id+"F0.wireOp",EDGE,"E19.1.3.0");Q3=makeQuery(id+"F0.imprint","IMPRINT",FACE,{"disambiguationData":[TD([[makeQuery(id+"F0.imprint","IMPRINT",EDGE,{"derivedFrom":subQ0}),-1.0]])]});}
            var Q4;
            {var subQ0=sQuery(id+"F0.wireOp",EDGE,"E19.1.4.0");Q4=makeQuery(id+"F0.imprint","IMPRINT",FACE,{"disambiguationData":[TD([[makeQuery(id+"F0.imprint","IMPRINT",EDGE,{"derivedFrom":subQ0}),-1.0]])]});}
            var Q5;
            {var subQ0=sQuery(id+"F0.wireOp",EDGE,"E19.1.5.0");Q5=makeQuery(id+"F0.imprint","IMPRINT",FACE,{"disambiguationData":[TD([[makeQuery(id+"F0.imprint","IMPRINT",EDGE,{"derivedFrom":subQ0}),-1.0]])]});}
            var Q6;
            Q6=makeQuery(id+"F0.imprint","IMPRINT",FACE,{"disambiguationData":[TD([[makeQuery(id+"F0.imprint","IMPRINT",EDGE,{"derivedFrom":sQuery(id+"F0.wireOp",EDGE,"E1.bottom")}),1.0]])]});
            extrude(context, id + "F1", {"entities" : qUnion([Q0, Q1, Q2, Q3, Q4, Q5, Q6]), "depth" : 3.17 * mm});
        }
        {
            var Q0;
            Q0=makeQuery(id+"F1.opExtrude","CAP_FACE",FACE,{"disambiguationData":[OSD([sQuery(id+"F0.wireOp",EDGE,"E1.bottom"),sQuery(id+"F0.wireOp",EDGE,"E1.top"),sQuery(id+"F0.wireOp",EDGE,"E1.left"),sQuery(id+"F0.wireOp",EDGE,"E1.right"),sQuery(id+"F0.wireOp",EDGE,"E2.0.1.1"),sQuery(id+"F0.wireOp",EDGE,"E2.0.1.2"),sQuery(id+"F0.wireOp",EDGE,"E2.0.1.3"),sQuery(id+"F0.wireOp",EDGE,"E2.0.1.4"),sQuery(id+"F0.wireOp",EDGE,"E2.1.0.1"),sQuery(id+"F0.wireOp",EDGE,"E2.1.0.2"),sQuery(id+"F0.wireOp",EDGE,"E2.1.0.3"),sQuery(id+"F0.wireOp",EDGE,"E2.1.0.4"),sQuery(id+"F0.wireOp",EDGE,"E2.1.1.1"),sQuery(id+"F0.wireOp",EDGE,"E2.1.1.2"),sQuery(id+"F0.wireOp",EDGE,"E2.1.1.3"),sQuery(id+"F0.wireOp",EDGE,"E2.1.1.4"),sQuery(id+"F0.wireOp",EDGE,"E3.1.0"),sQuery(id+"F0.wireOp",EDGE,"E3.1.1"),sQuery(id+"F0.wireOp",EDGE,"E3.1.3"),sQuery(id+"F0.wireOp",EDGE,"E3.1.4"),sQuery(id+"F0.wireOp",EDGE,"E3.1.5"),sQuery(id+"F0.wireOp",EDGE,"E3.1.7"),sQuery(id+"F0.wireOp",EDGE,"E3.1.9"),sQuery(id+"F0.wireOp",EDGE,"E3.1.10"),sQuery(id+"F0.wireOp",EDGE,"E3.1.14"),sQuery(id+"F0.wireOp",EDGE,"E3.1.15"),sQuery(id+"F0.wireOp",EDGE,"E3.1.16"),sQuery(id+"F0.wireOp",EDGE,"E3.1.17"),sQuery(id+"F0.wireOp",EDGE,"E3.1.18"),sQuery(id+"F0.wireOp",EDGE,"E3.1.19"),sQuery(id+"F0.wireOp",EDGE,"E3.1.20"),sQuery(id+"F0.wireOp",EDGE,"E3.1.21"),sQuery(id+"F0.wireOp",EDGE,"E3.2.0"),sQuery(id+"F0.wireOp",EDGE,"E3.2.1"),sQuery(id+"F0.wireOp",EDGE,"E3.2.3"),sQuery(id+"F0.wireOp",EDGE,"E3.2.4"),sQuery(id+"F0.wireOp",EDGE,"E3.2.5"),sQuery(id+"F0.wireOp",EDGE,"E3.2.7"),sQuery(id+"F0.wireOp",EDGE,"E3.2.9"),sQuery(id+"F0.wireOp",EDGE,"E3.2.10"),sQuery(id+"F0.wireOp",EDGE,"E3.2.14"),sQuery(id+"F0.wireOp",EDGE,"E3.2.15"),sQuery(id+"F0.wireOp",EDGE,"E3.2.16"),sQuery(id+"F0.wireOp",EDGE,"E3.2.17"),sQuery(id+"F0.wireOp",EDGE,"E3.2.18"),sQuery(id+"F0.wireOp",EDGE,"E3.2.19"),sQuery(id+"F0.wireOp",EDGE,"E3.2.20"),sQuery(id+"F0.wireOp",EDGE,"E3.2.21"),sQuery(id+"F0.wireOp",EDGE,"E3.3.0"),sQuery(id+"F0.wireOp",EDGE,"E3.3.1"),sQuery(id+"F0.wireOp",EDGE,"E3.3.3"),sQuery(id+"F0.wireOp",EDGE,"E3.3.4"),sQuery(id+"F0.wireOp",EDGE,"E3.3.5"),sQuery(id+"F0.wireOp",EDGE,"E3.3.7"),sQuery(id+"F0.wireOp",EDGE,"E3.3.9"),sQuery(id+"F0.wireOp",EDGE,"E3.3.10"),sQuery(id+"F0.wireOp",EDGE,"E3.3.14"),sQuery(id+"F0.wireOp",EDGE,"E3.3.15"),sQuery(id+"F0.wireOp",EDGE,"E3.3.16"),sQuery(id+"F0.wireOp",EDGE,"E3.3.17"),sQuery(id+"F0.wireOp",EDGE,"E3.3.18"),sQuery(id+"F0.wireOp",EDGE,"E3.3.19"),sQuery(id+"F0.wireOp",EDGE,"E3.3.20"),sQuery(id+"F0.wireOp",EDGE,"E3.3.21"),sQuery(id+"F0.wireOp",EDGE,"E3.4.0"),sQuery(id+"F0.wireOp",EDGE,"E3.4.1"),sQuery(id+"F0.wireOp",EDGE,"E3.4.3"),sQuery(id+"F0.wireOp",EDGE,"E3.4.4"),sQuery(id+"F0.wireOp",EDGE,"E3.4.5"),sQuery(id+"F0.wireOp",EDGE,"E3.4.7"),sQuery(id+"F0.wireOp",EDGE,"E3.4.9"),sQuery(id+"F0.wireOp",EDGE,"E3.4.10"),sQuery(id+"F0.wireOp",EDGE,"E3.4.14"),sQuery(id+"F0.wireOp",EDGE,"E3.4.15"),sQuery(id+"F0.wireOp",EDGE,"E3.4.16"),sQuery(id+"F0.wireOp",EDGE,"E3.4.17"),sQuery(id+"F0.wireOp",EDGE,"E3.4.18"),sQuery(id+"F0.wireOp",EDGE,"E3.4.19"),sQuery(id+"F0.wireOp",EDGE,"E3.4.20"),sQuery(id+"F0.wireOp",EDGE,"E3.4.21"),sQuery(id+"F0.wireOp",EDGE,"E3.5.0"),sQuery(id+"F0.wireOp",EDGE,"E3.5.1"),sQuery(id+"F0.wireOp",EDGE,"E3.5.3"),sQuery(id+"F0.wireOp",EDGE,"E3.5.4"),sQuery(id+"F0.wireOp",EDGE,"E3.5.5"),sQuery(id+"F0.wireOp",EDGE,"E3.5.7"),sQuery(id+"F0.wireOp",EDGE,"E3.5.9"),sQuery(id+"F0.wireOp",EDGE,"E3.5.10"),sQuery(id+"F0.wireOp",EDGE,"E3.5.14"),sQuery(id+"F0.wireOp",EDGE,"E3.5.15"),sQuery(id+"F0.wireOp",EDGE,"E3.5.16"),sQuery(id+"F0.wireOp",EDGE,"E3.5.17"),sQuery(id+"F0.wireOp",EDGE,"E3.5.18"),sQuery(id+"F0.wireOp",EDGE,"E3.5.19"),sQuery(id+"F0.wireOp",EDGE,"E3.5.20"),sQuery(id+"F0.wireOp",EDGE,"E3.5.21"),sQuery(id+"F0.wireOp",EDGE,"E5"),sQuery(id+"F0.wireOp",EDGE,"E6.1.0"),sQuery(id+"F0.wireOp",EDGE,"E6.2.0"),sQuery(id+"F0.wireOp",EDGE,"E6.3.0"),sQuery(id+"F0.wireOp",EDGE,"E7.1.0.2"),sQuery(id+"F0.wireOp",EDGE,"E7.4.0.2"),sQuery(id+"F0.wireOp",EDGE,"E7.7.0.2"),sQuery(id+"F0.wireOp",EDGE,"E7.10.0.2"),sQuery(id+"F0.wireOp",EDGE,"E7.1.1.2"),sQuery(id+"F0.wireOp",EDGE,"E7.4.1.2"),sQuery(id+"F0.wireOp",EDGE,"E7.7.1.2"),sQuery(id+"F0.wireOp",EDGE,"E7.10.1.2"),sQuery(id+"F0.wireOp",EDGE,"E8.1.0.3"),sQuery(id+"F0.wireOp",EDGE,"E8.4.0.3"),sQuery(id+"F0.wireOp",EDGE,"E8.7.0.3"),sQuery(id+"F0.wireOp",EDGE,"E8.10.0.3"),sQuery(id+"F0.wireOp",EDGE,"E8.1.1.3"),sQuery(id+"F0.wireOp",EDGE,"E8.4.1.3"),sQuery(id+"F0.wireOp",EDGE,"E8.7.1.3"),sQuery(id+"F0.wireOp",EDGE,"E8.10.1.3"),sQuery(id+"F0.wireOp",EDGE,"E9.1.4"),sQuery(id+"F0.wireOp",EDGE,"E9.1.5"),sQuery(id+"F0.wireOp",EDGE,"E9.1.6"),sQuery(id+"F0.wireOp",EDGE,"E9.1.7"),sQuery(id+"F0.wireOp",EDGE,"E9.1.8"),sQuery(id+"F0.wireOp",EDGE,"E9.1.9"),sQuery(id+"F0.wireOp",EDGE,"E9.1.10"),sQuery(id+"F0.wireOp",EDGE,"E9.1.11"),sQuery(id+"F0.wireOp",EDGE,"E9.1.12"),sQuery(id+"F0.wireOp",EDGE,"E9.1.13"),sQuery(id+"F0.wireOp",EDGE,"E9.1.14"),sQuery(id+"F0.wireOp",EDGE,"E9.1.15"),sQuery(id+"F0.wireOp",EDGE,"E9.1.16"),sQuery(id+"F0.wireOp",EDGE,"E9.1.17"),sQuery(id+"F0.wireOp",EDGE,"E9.1.18"),sQuery(id+"F0.wireOp",EDGE,"E9.1.19"),sQuery(id+"F0.wireOp",EDGE,"E9.2.4"),sQuery(id+"F0.wireOp",EDGE,"E9.2.5"),sQuery(id+"F0.wireOp",EDGE,"E9.2.6"),sQuery(id+"F0.wireOp",EDGE,"E9.2.7"),sQuery(id+"F0.wireOp",EDGE,"E9.2.8"),sQuery(id+"F0.wireOp",EDGE,"E9.2.9"),sQuery(id+"F0.wireOp",EDGE,"E9.2.10"),sQuery(id+"F0.wireOp",EDGE,"E9.2.11"),sQuery(id+"F0.wireOp",EDGE,"E9.2.12"),sQuery(id+"F0.wireOp",EDGE,"E9.2.13"),sQuery(id+"F0.wireOp",EDGE,"E9.2.14"),sQuery(id+"F0.wireOp",EDGE,"E9.2.15"),sQuery(id+"F0.wireOp",EDGE,"E9.2.16"),sQuery(id+"F0.wireOp",EDGE,"E9.2.17"),sQuery(id+"F0.wireOp",EDGE,"E9.2.18"),sQuery(id+"F0.wireOp",EDGE,"E9.2.19"),sQuery(id+"F0.wireOp",EDGE,"E9.3.4"),sQuery(id+"F0.wireOp",EDGE,"E9.3.5"),sQuery(id+"F0.wireOp",EDGE,"E9.3.6"),sQuery(id+"F0.wireOp",EDGE,"E9.3.7"),sQuery(id+"F0.wireOp",EDGE,"E9.3.8"),sQuery(id+"F0.wireOp",EDGE,"E9.3.9"),sQuery(id+"F0.wireOp",EDGE,"E9.3.10"),sQuery(id+"F0.wireOp",EDGE,"E9.3.11"),sQuery(id+"F0.wireOp",EDGE,"E9.3.12"),sQuery(id+"F0.wireOp",EDGE,"E9.3.13"),sQuery(id+"F0.wireOp",EDGE,"E9.3.14"),sQuery(id+"F0.wireOp",EDGE,"E9.3.15"),sQuery(id+"F0.wireOp",EDGE,"E9.3.16"),sQuery(id+"F0.wireOp",EDGE,"E9.3.17"),sQuery(id+"F0.wireOp",EDGE,"E9.3.18"),sQuery(id+"F0.wireOp",EDGE,"E9.3.19"),sQuery(id+"F0.wireOp",EDGE,"E9.4.4"),sQuery(id+"F0.wireOp",EDGE,"E9.4.5"),sQuery(id+"F0.wireOp",EDGE,"E9.4.6"),sQuery(id+"F0.wireOp",EDGE,"E9.4.7"),sQuery(id+"F0.wireOp",EDGE,"E9.4.8"),sQuery(id+"F0.wireOp",EDGE,"E9.4.9"),sQuery(id+"F0.wireOp",EDGE,"E9.4.10"),sQuery(id+"F0.wireOp",EDGE,"E9.4.11"),sQuery(id+"F0.wireOp",EDGE,"E9.4.12"),sQuery(id+"F0.wireOp",EDGE,"E9.4.13"),sQuery(id+"F0.wireOp",EDGE,"E9.4.14"),sQuery(id+"F0.wireOp",EDGE,"E9.4.15"),sQuery(id+"F0.wireOp",EDGE,"E9.4.16"),sQuery(id+"F0.wireOp",EDGE,"E9.4.17"),sQuery(id+"F0.wireOp",EDGE,"E9.4.18"),sQuery(id+"F0.wireOp",EDGE,"E9.4.19"),sQuery(id+"F0.wireOp",EDGE,"E9.5.4"),sQuery(id+"F0.wireOp",EDGE,"E9.5.5"),sQuery(id+"F0.wireOp",EDGE,"E9.5.6"),sQuery(id+"F0.wireOp",EDGE,"E9.5.7"),sQuery(id+"F0.wireOp",EDGE,"E9.5.8"),sQuery(id+"F0.wireOp",EDGE,"E9.5.9"),sQuery(id+"F0.wireOp",EDGE,"E9.5.10"),sQuery(id+"F0.wireOp",EDGE,"E9.5.11"),sQuery(id+"F0.wireOp",EDGE,"E9.5.12"),sQuery(id+"F0.wireOp",EDGE,"E9.5.13"),sQuery(id+"F0.wireOp",EDGE,"E9.5.14"),sQuery(id+"F0.wireOp",EDGE,"E9.5.15"),sQuery(id+"F0.wireOp",EDGE,"E9.5.16"),sQuery(id+"F0.wireOp",EDGE,"E9.5.17"),sQuery(id+"F0.wireOp",EDGE,"E9.5.18"),sQuery(id+"F0.wireOp",EDGE,"E9.5.19"),sQuery(id+"F0.wireOp",EDGE,"E10"),sQuery(id+"F0.wireOp",EDGE,"E11"),sQuery(id+"F0.wireOp",EDGE,"E12"),sQuery(id+"F0.wireOp",EDGE,"E14.1.1"),sQuery(id+"F0.wireOp",EDGE,"E14.1.2"),sQuery(id+"F0.wireOp",EDGE,"E14.1.3"),sQuery(id+"F0.wireOp",EDGE,"E14.2.1"),sQuery(id+"F0.wireOp",EDGE,"E14.2.2"),sQuery(id+"F0.wireOp",EDGE,"E14.2.3"),sQuery(id+"F0.wireOp",EDGE,"E14.3.1"),sQuery(id+"F0.wireOp",EDGE,"E14.3.2"),sQuery(id+"F0.wireOp",EDGE,"E14.3.3"),sQuery(id+"F0.wireOp",EDGE,"E14.4.1"),sQuery(id+"F0.wireOp",EDGE,"E14.4.2"),sQuery(id+"F0.wireOp",EDGE,"E14.4.3"),sQuery(id+"F0.wireOp",EDGE,"E14.5.1"),sQuery(id+"F0.wireOp",EDGE,"E14.5.2"),sQuery(id+"F0.wireOp",EDGE,"E14.5.3"),sQuery(id+"F0.wireOp",EDGE,"E15"),sQuery(id+"F0.wireOp",EDGE,"E17"),sQuery(id+"F0.wireOp",EDGE,"E18.1.0"),sQuery(id+"F0.wireOp",EDGE,"E18.1.1"),sQuery(id+"F0.wireOp",EDGE,"E18.2.0"),sQuery(id+"F0.wireOp",EDGE,"E18.2.1"),sQuery(id+"F0.wireOp",EDGE,"E19.1.3.0"),sQuery(id+"F0.wireOp",EDGE,"E19.3.3.0"),sQuery(id+"F0.wireOp",EDGE,"E19.1.4.0"),sQuery(id+"F0.wireOp",EDGE,"E19.3.4.0"),sQuery(id+"F0.wireOp",EDGE,"E19.1.5.0"),sQuery(id+"F0.wireOp",EDGE,"E19.3.5.0"),sQuery(id+"F0.wireOp",EDGE,"E20"),sQuery(id+"F0.wireOp",EDGE,"E21"),sQuery(id+"F0.wireOp",EDGE,"E22"),sQuery(id+"F0.wireOp",EDGE,"E23.1.0"),sQuery(id+"F0.wireOp",EDGE,"E23.1.1"),sQuery(id+"F0.wireOp",EDGE,"E23.1.2"),sQuery(id+"F0.wireOp",EDGE,"E23.2.0"),sQuery(id+"F0.wireOp",EDGE,"E23.2.1"),sQuery(id+"F0.wireOp",EDGE,"E23.2.2"),sQuery(id+"F0.wireOp",EDGE,"E23.3.0"),sQuery(id+"F0.wireOp",EDGE,"E23.3.1"),sQuery(id+"F0.wireOp",EDGE,"E23.3.2"),sQuery(id+"F0.wireOp",EDGE,"E23.4.0"),sQuery(id+"F0.wireOp",EDGE,"E23.4.1"),sQuery(id+"F0.wireOp",EDGE,"E23.4.2"),sQuery(id+"F0.wireOp",EDGE,"E23.5.2"),sQuery(id+"F0.wireOp",EDGE,"E24"),sQuery(id+"F0.wireOp",EDGE,"E25")])],"isStart":false});
            var sketch = newSketch(context, id + "F2", { "sketchPlane" : qUnion([Q0])});
            skLineSegment(sketch, "E26.bottom", {"start": v(7.5, 162.99) * mm, "end": v(-7.5, 162.99) * mm});
            skLineSegment(sketch, "E26.top", {"start": v(7.5, 72.99) * mm, "end": v(-7.5, 72.99) * mm});
            skLineSegment(sketch, "E26.left", {"start": v(7.5, 162.99) * mm, "end": v(7.5, 72.99) * mm});
            skLineSegment(sketch, "E26.right", {"start": v(-7.5, 162.99) * mm, "end": v(-7.5, 72.99) * mm});
            skPoint(sketch, "E26.middle", {"position": v(0, 117.99) * mm});
            skPoint(sketch, "E27.1.0", {"position": v(-102.18, 59) * mm});
            skLineSegment(sketch, "E27.1.1", {"start": v(-137.4, 87.99) * mm, "end": v(-144.9, 75) * mm});
            skLineSegment(sketch, "E27.1.2", {"start": v(-144.9, 75) * mm, "end": v(-66.96, 30) * mm});
            skLineSegment(sketch, "E27.1.3", {"start": v(-137.4, 87.99) * mm, "end": v(-59.46, 42.99) * mm});
            skLineSegment(sketch, "E27.1.4", {"start": v(-59.46, 42.99) * mm, "end": v(-66.96, 30) * mm});
            skPoint(sketch, "E27.2.0", {"position": v(-102.18, -59) * mm});
            skLineSegment(sketch, "E27.2.1", {"start": v(-144.9, -75) * mm, "end": v(-137.4, -87.99) * mm});
            skLineSegment(sketch, "E27.2.2", {"start": v(-137.4, -87.99) * mm, "end": v(-59.46, -42.99) * mm});
            skLineSegment(sketch, "E27.2.3", {"start": v(-144.9, -75) * mm, "end": v(-66.96, -30) * mm});
            skLineSegment(sketch, "E27.2.4", {"start": v(-66.96, -30) * mm, "end": v(-59.46, -42.99) * mm});
            skPoint(sketch, "E27.3.0", {"position": v(0, -117.99) * mm});
            skLineSegment(sketch, "E27.3.1", {"start": v(-7.5, -162.99) * mm, "end": v(7.5, -162.99) * mm});
            skLineSegment(sketch, "E27.3.2", {"start": v(7.5, -162.99) * mm, "end": v(7.5, -72.99) * mm});
            skLineSegment(sketch, "E27.3.3", {"start": v(-7.5, -162.99) * mm, "end": v(-7.5, -72.99) * mm});
            skLineSegment(sketch, "E27.3.4", {"start": v(-7.5, -72.99) * mm, "end": v(7.5, -72.99) * mm});
            skPoint(sketch, "E27.4.0", {"position": v(102.18, -59) * mm});
            skLineSegment(sketch, "E27.4.1", {"start": v(137.4, -87.99) * mm, "end": v(144.9, -75) * mm});
            skLineSegment(sketch, "E27.4.2", {"start": v(144.9, -75) * mm, "end": v(66.96, -30) * mm});
            skLineSegment(sketch, "E27.4.3", {"start": v(137.4, -87.99) * mm, "end": v(59.46, -42.99) * mm});
            skLineSegment(sketch, "E27.4.4", {"start": v(59.46, -42.99) * mm, "end": v(66.96, -30) * mm});
            skPoint(sketch, "E27.5.0", {"position": v(102.18, 59) * mm});
            skLineSegment(sketch, "E27.5.1", {"start": v(144.9, 75) * mm, "end": v(137.4, 87.99) * mm});
            skLineSegment(sketch, "E27.5.2", {"start": v(137.4, 87.99) * mm, "end": v(59.46, 42.99) * mm});
            skLineSegment(sketch, "E27.5.3", {"start": v(144.9, 75) * mm, "end": v(66.96, 30) * mm});
            skLineSegment(sketch, "E27.5.4", {"start": v(66.96, 30) * mm, "end": v(59.46, 42.99) * mm});
            skPoint(sketch, "E27.center", {"position": v(0, 0) * mm});
            skSolve(sketch);
        }
        {
            var Q0;
            Q0=makeQuery(id+"F2.imprint","IMPRINT",FACE,{"disambiguationData":[TD([[makeQuery(id+"F2.imprint","IMPRINT",EDGE,{"derivedFrom":sQuery(id+"F2.wireOp",EDGE,"E27.1.1")}),-1.0]])]});
            var Q1;
            Q1=makeQuery(id+"F2.imprint","IMPRINT",FACE,{"disambiguationData":[TD([[makeQuery(id+"F2.imprint","IMPRINT",EDGE,{"derivedFrom":sQuery(id+"F2.wireOp",EDGE,"E26.bottom")}),1.0]])]});
            var Q2;
            Q2=makeQuery(id+"F2.imprint","IMPRINT",FACE,{"disambiguationData":[TD([[makeQuery(id+"F2.imprint","IMPRINT",EDGE,{"derivedFrom":sQuery(id+"F2.wireOp",EDGE,"E27.5.1")}),-1.0]])]});
            var Q3;
            Q3=makeQuery(id+"F2.imprint","IMPRINT",FACE,{"disambiguationData":[TD([[makeQuery(id+"F2.imprint","IMPRINT",EDGE,{"derivedFrom":sQuery(id+"F2.wireOp",EDGE,"E27.4.1")}),-1.0]])]});
            var Q4;
            Q4=makeQuery(id+"F2.imprint","IMPRINT",FACE,{"disambiguationData":[TD([[makeQuery(id+"F2.imprint","IMPRINT",EDGE,{"derivedFrom":sQuery(id+"F2.wireOp",EDGE,"E27.3.1")}),-1.0]])]});
            var Q5;
            Q5=makeQuery(id+"F2.imprint","IMPRINT",FACE,{"disambiguationData":[TD([[makeQuery(id+"F2.imprint","IMPRINT",EDGE,{"derivedFrom":sQuery(id+"F2.wireOp",EDGE,"E27.2.1")}),-1.0]])]});
            extrude(context, id + "F3", {"entities" : qUnion([Q0, Q1, Q2, Q3, Q4, Q5]), "operationType" : NewBodyOperationType.REMOVE, "oppositeDirection" : true, "depth" : 25 * mm});
        }
    });
